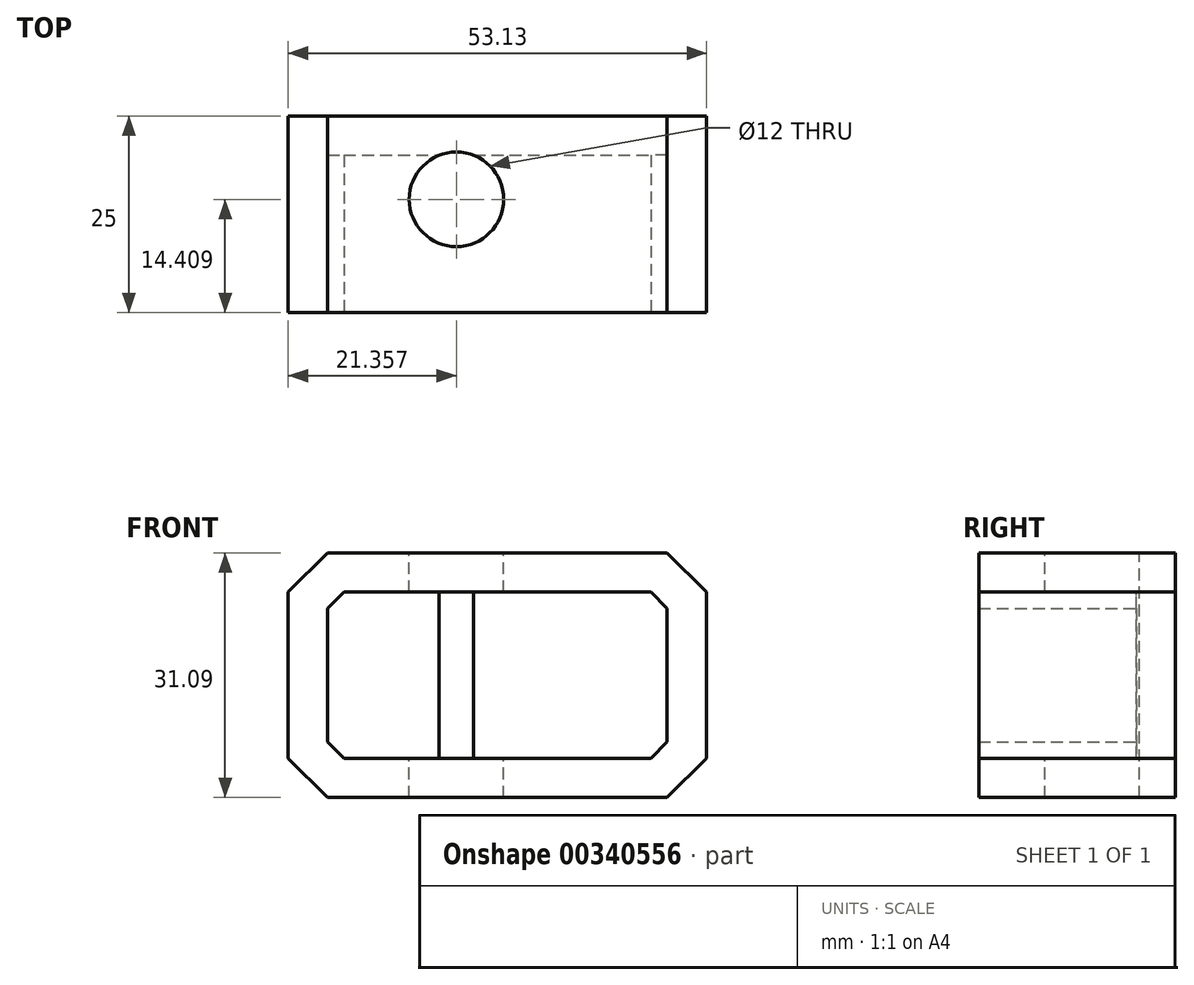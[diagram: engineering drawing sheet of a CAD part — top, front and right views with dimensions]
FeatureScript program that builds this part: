
annotation { "Feature Type Name" : "Feature", "Feature Type Description" : "" }
export const myFeature = defineFeature(function(context is Context, id is Id, definition is map)
    precondition{}
    {
        {
            var Q0;
            Q0=qCreatedBy(makeId("Front.planeOp"),FACE);
            var sketch = newSketch(context, id + "F0", { "sketchPlane" : qUnion([Q0])});
            skLineSegment(sketch, "E0.bottom", {"start": v(-59.28, 11.27) * mm, "end": v(-6.15, 11.27) * mm});
            skLineSegment(sketch, "E0.top", {"start": v(-59.28, -19.82) * mm, "end": v(-6.15, -19.82) * mm});
            skLineSegment(sketch, "E0.left", {"start": v(-59.28, 11.27) * mm, "end": v(-59.28, -19.82) * mm});
            skLineSegment(sketch, "E0.right", {"start": v(-6.15, 11.27) * mm, "end": v(-6.15, -19.82) * mm});
            skSolve(sketch);
        }
        {
            var Q0;
            Q0=makeQuery(id+"F0.imprint","IMPRINT",FACE,{"disambiguationData":[TD([[makeQuery(id+"F0.imprint","IMPRINT",EDGE,{"derivedFrom":sQuery(id+"F0.wireOp",EDGE,"E0.bottom")}),-1.0]])]});
            extrude(context, id + "F1", {"entities" : qUnion([Q0]), "depth" : 25 * mm});
        }
        {
            var Q0;
            Q0=makeQuery(id+"F1.opExtrude","SWEPT_EDGE",EDGE,{"disambiguationData":[OSD([sQuery(id+"F0.wireOp",EDGE,"E0.bottom"),sQuery(id+"F0.wireOp",EDGE,"E0.right")])]});
            var Q1;
            Q1=makeQuery(id+"F1.opExtrude","SWEPT_EDGE",EDGE,{"disambiguationData":[OSD([sQuery(id+"F0.wireOp",EDGE,"E0.bottom"),sQuery(id+"F0.wireOp",EDGE,"E0.left")])]});
            var Q2;
            Q2=makeQuery(id+"F1.opExtrude","SWEPT_EDGE",EDGE,{"disambiguationData":[OSD([sQuery(id+"F0.wireOp",EDGE,"E0.top"),sQuery(id+"F0.wireOp",EDGE,"E0.right")])]});
            var Q3;
            Q3=makeQuery(id+"F1.opExtrude","SWEPT_EDGE",EDGE,{"disambiguationData":[OSD([sQuery(id+"F0.wireOp",EDGE,"E0.top"),sQuery(id+"F0.wireOp",EDGE,"E0.left")])]});
            chamfer(context, id + "F2", {"entities" : qUnion([Q0, Q1, Q2, Q3]), "width" : 5 * mm, "tangentPropagation" : true});
        }
        {
            var Q0;
            Q0=makeQuery(id+"F1.opExtrude","CAP_FACE",FACE,{"disambiguationData":[OSD([sQuery(id+"F0.wireOp",EDGE,"E0.bottom"),sQuery(id+"F0.wireOp",EDGE,"E0.top"),sQuery(id+"F0.wireOp",EDGE,"E0.left"),sQuery(id+"F0.wireOp",EDGE,"E0.right")])],"isStart":false});
            shell(context, id + "F3", {"entities" : qUnion([Q0]), "thickness" : 5 * mm});
        }
        {
            var Q0;
            Q0=makeQuery(id+"F1.opExtrude","SWEPT_FACE",FACE,{"disambiguationData":[OSD([sQuery(id+"F0.wireOp",EDGE,"E0.bottom")])]});
            var sketch = newSketch(context, id + "F4", { "sketchPlane" : qUnion([Q0])});
            skCircle(sketch, "E1", {"center": v(-37.92, -10.6) * mm, "radius": 5.56 * mm});
            skSolve(sketch);
        }
        {
            var Q0;
            Q0=sQuery(id+"F4.wireOp",VERTEX,"E1.center");
            var Q1;
            Q1=makeQuery(id+"F1.opExtrude","SWEPT_BODY",BODY,{"disambiguationData":[OSD([sQuery(id+"F0.wireOp",EDGE,"E0.bottom"),sQuery(id+"F0.wireOp",EDGE,"E0.top"),sQuery(id+"F0.wireOp",EDGE,"E0.left"),sQuery(id+"F0.wireOp",EDGE,"E0.right")])]});
            hole(context, id + "F5", {"style" : HoleStyle.SIMPLE, "endStyle" : HoleEndStyle.THROUGH, "holeDiameter" : 12 * mm, "tappedDepth" : 12 * mm, "tapClearance" : 3, "startFromSketch" : true, "locations" : qUnion([Q0]), "scope" : qUnion([Q1])});
        }
    });
